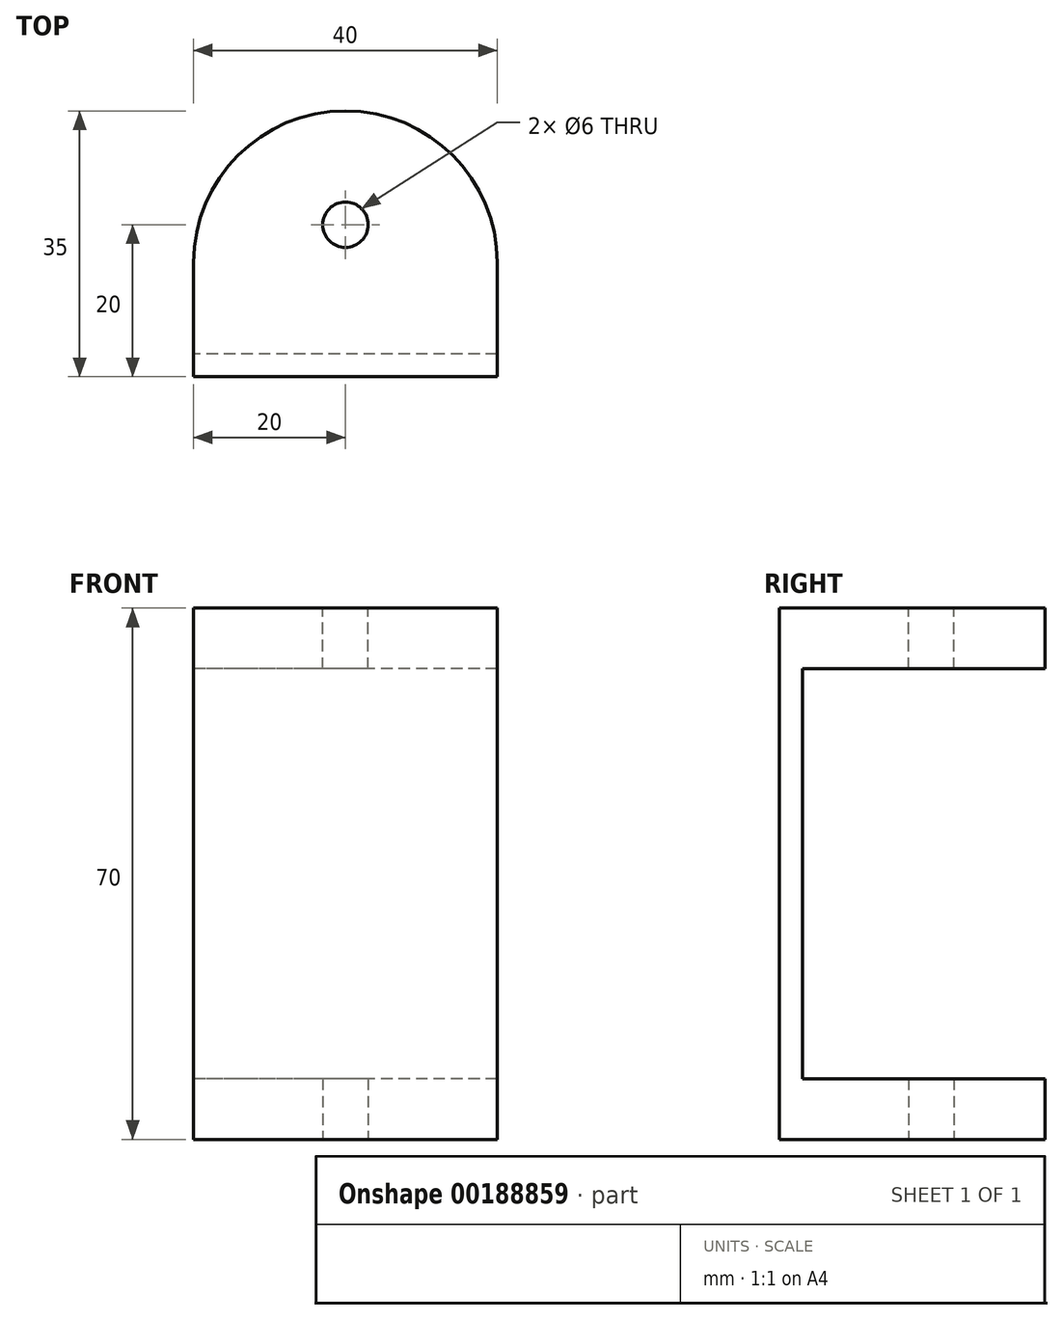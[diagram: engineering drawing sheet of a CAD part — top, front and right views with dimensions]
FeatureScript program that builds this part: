
annotation { "Feature Type Name" : "Feature", "Feature Type Description" : "" }
export const myFeature = defineFeature(function(context is Context, id is Id, definition is map)
    precondition{}
    {
        {
            var Q0;
            Q0=qCreatedBy(makeId("Top.planeOp"),FACE);
            var sketch = newSketch(context, id + "F0", { "sketchPlane" : qUnion([Q0])});
            skLineSegment(sketch, "E0.bottom", {"start": v(20, -17.5) * mm, "end": v(-20, -17.5) * mm});
            skLineSegment(sketch, "E0.top", {"start": v(20, 17.5) * mm, "end": v(-20, 17.5) * mm});
            skLineSegment(sketch, "E0.left", {"start": v(20, -17.5) * mm, "end": v(20, 17.5) * mm});
            skLineSegment(sketch, "E0.right", {"start": v(-20, -17.5) * mm, "end": v(-20, 17.5) * mm});
            skPoint(sketch, "E0.middle", {"position": v(0, 0) * mm});
            skLineSegment(sketch, "E1", {"start": v(0, 17.5) * mm, "end": v(0, 2.5) * mm, "construction": true});
            skPoint(sketch, "E1.endSnap0", {"position": v(0, 17.5) * mm});
            skCircle(sketch, "E2", {"center": v(0, 2.5) * mm, "radius": 3 * mm});
            skSolve(sketch);
        }
        {
            var Q0;
            Q0=makeQuery(id+"F0.imprint","IMPRINT",FACE,{"disambiguationData":[TD([[makeQuery(id+"F0.imprint","IMPRINT",EDGE,{"derivedFrom":sQuery(id+"F0.wireOp",EDGE,"E0.bottom")}),-1.0]])]});
            extrude(context, id + "F1", {"entities" : qUnion([Q0]), "depth" : 8 * mm});
        }
        {
            var Q0;
            Q0=makeQuery(id+"F0.imprint","IMPRINT",FACE,{"disambiguationData":[TD([[makeQuery(id+"F0.imprint","IMPRINT",EDGE,{"derivedFrom":sQuery(id+"F0.wireOp",EDGE,"E2")}),1.0]])]});
            extrude(context, id + "F2", {"entities" : qUnion([Q0]), "operationType" : NewBodyOperationType.ADD, "depth" : 2 * mm});
        }
        {
            var Q0;
            Q0=makeQuery(id+"F1.opExtrude","SWEPT_FACE",FACE,{"disambiguationData":[OSD([sQuery(id+"F0.wireOp",EDGE,"E0.bottom")])]});
            var sketch = newSketch(context, id + "F3", { "sketchPlane" : qUnion([Q0])});
            skLineSegment(sketch, "E3.bottom", {"start": v(-20, 0) * mm, "end": v(20, 0) * mm});
            skLineSegment(sketch, "E3.top", {"start": v(-20, 35) * mm, "end": v(20, 35) * mm});
            skLineSegment(sketch, "E3.left", {"start": v(-20, 0) * mm, "end": v(-20, 35) * mm});
            skLineSegment(sketch, "E3.right", {"start": v(20, 0) * mm, "end": v(20, 35) * mm});
            skSolve(sketch);
        }
        {
            var Q0;
            {var subQ0=sQuery(id+"F3.wireOp",EDGE,"E3.top");Q0=makeQuery(id+"F3.imprint","IMPRINT",FACE,{"disambiguationData":[TD([[makeQuery(id+"F3.imprint","IMPRINT",EDGE,{"derivedFrom":subQ0}),-1.0]])]});}
            extrude(context, id + "F4", {"entities" : qUnion([Q0]), "operationType" : NewBodyOperationType.ADD, "oppositeDirection" : true, "depth" : 3 * mm});
        }
        {
            var Q0;
            Q0=makeQuery(id+"F1.opExtrude","SWEPT_EDGE",EDGE,{"disambiguationData":[OSD([sQuery(id+"F0.wireOp",EDGE,"E0.top"),sQuery(id+"F0.wireOp",EDGE,"E0.right")])]});
            fillet(context, id + "F5", {"entities" : qUnion([Q0]), "radius" : 20 * mm, "tangentPropagation" : true, "allowEdgeOverflow" : false});
        }
        {
            var Q0;
            Q0=makeQuery(id+"F1.opExtrude","SWEPT_EDGE",EDGE,{"disambiguationData":[OSD([sQuery(id+"F0.wireOp",EDGE,"E0.top"),sQuery(id+"F0.wireOp",EDGE,"E0.left")])]});
            fillet(context, id + "F6", {"entities" : qUnion([Q0]), "radius" : 20 * mm, "tangentPropagation" : true, "allowEdgeOverflow" : false});
        }
        {
            var Q0;
            Q0=makeQuery(id+"F1.opExtrude","SWEPT_BODY",BODY,{"disambiguationData":[OSD([sQuery(id+"F0.wireOp",EDGE,"E0.bottom"),sQuery(id+"F0.wireOp",EDGE,"E0.top"),sQuery(id+"F0.wireOp",EDGE,"E0.left"),sQuery(id+"F0.wireOp",EDGE,"E0.right"),sQuery(id+"F0.wireOp",EDGE,"E2")])]});
            var Q1;
            Q1=makeQuery(id+"F4.opExtrude","SWEPT_FACE",FACE,{"disambiguationData":[OSD([sQuery(id+"F3.wireOp",EDGE,"E3.top")])]});
            mirror(context, id + "F7", {"operationType" : NewBodyOperationType.ADD, "entities" : qUnion([Q0]), "mirrorPlane" : qUnion([Q1])});
        }
        {
            var Q0;
            Q0=makeQuery(id+"F2.opExtrude","CAP_FACE",FACE,{"disambiguationData":[OSD([sQuery(id+"F0.wireOp",EDGE,"E2")])],"isStart":false});
            extrude(context, id + "F8", {"entities" : qUnion([Q0]), "operationType" : NewBodyOperationType.REMOVE, "endBound" : BoundingType.THROUGH_ALL, "oppositeDirection" : true, "depth" : 25 * mm});
        }
        {
            var Q0;
            Q0=makeQuery(id+"F7.opPattern","COPY",FACE,{"derivedFrom":makeQuery(id+"F2.opExtrude","CAP_FACE",FACE,{"disambiguationData":[OSD([sQuery(id+"F0.wireOp",EDGE,"E2")])],"isStart":false}),"instanceName":"1"});
            extrude(context, id + "F9", {"entities" : qUnion([Q0]), "operationType" : NewBodyOperationType.REMOVE, "endBound" : BoundingType.THROUGH_ALL, "oppositeDirection" : true, "depth" : 25 * mm});
        }
    });
